# Revit family: Casement_41_C_Side_Hung_SD_Standard
name_source: partatom
category: Windows
revit_build: Autodesk Revit 2014 (Build: 20130308_1515(x64)
units: mm (PartAtom-declared; Revit-internal decimal feet)

## types (12) — shared parameters
Corrected Mullion Configuration = 2 mm  [stored 0.00656168 ft]
Custom Sash Width = 502 mm
Description = Window 41mm, Type C, Side hung, Standard sash
Frame Profile Thickness = 41 mm  [stored 0.134514 ft]
Heavy Duty Sash = No
Limit Fixed Pane Height Max = 3000 mm  [stored 9.84252 ft]
Limit Fixed Pane Height Min = 200 mm  [stored 0.656168 ft]
Limit Fixed Pane Width Max = 3000 mm  [stored 9.84252 ft]
Limit Fixed Pane Width Min = 200 mm  [stored 0.656168 ft]
Limit Sash Height Max = 1500 mm  [stored 4.92126 ft]
Limit Sash Height Min = 300 mm  [stored 0.984252 ft]
Limit Sash Width Max = 700 mm  [stored 2.29659 ft]
Limit Sash Width Min = 300 mm  [stored 0.984252 ft]
Limit Window Height Max = 1588 mm
Limit Window Height Min = 388 mm
Manufacturer = Crealco
Max System DG Unit Thickness = 25 mm  [stored 0.082021 ft]
Model = Casement 41
Rough Width = 3 mm  [stored 0.00984252 ft]
Sash Side Gap = 44 mm
Standard Mullion Different = No
Standard Sash = Yes
URL = http://www.crealco.co.za
Wall Closure = By host
zero-valued in all types: Custom Frame Offset From Exterior

## per-type parameters (varying)
| type | Clearvue Insulated LowE SHGC Value | Clearvue Insulated LowE U Value | Clearvue Insulated SHGC Value | Clearvue Insulated U Value | Clearvue SHGC Value | Clearvue U Value | Custom Windload | Custom Window Height | Custom Window Width | Energy Advantage SHGC Value | Energy Advantage U Value | Intruderprufe Insulated LowE SHGC Value | Intruderprufe Insulated LowE U Value | Intruderprufe Insulated SHGC Value | Intruderprufe Insulated U Value | Intruderprufe LowE SHGC Value | Intruderprufe LowE U Value | Intruderprufe SHGC Value | Intruderprufe U Value | Toughened Safety SHGC Value | Toughened Safety U Value |
| 41-1809SS-SD-1000Pa | 0.737 | 4.46 | 0.737 | 4.54 | 0.544 | 6.03 | 1000 mm  [stored 3.28084 ft] | 890 mm  [stored 2.91995 ft] | 1790 mm  [stored 5.8727 ft] | 0.49 | 4.86 | 0.612 | 3.2 | 0.612 | 3.26 | 0.456 | 4.74 | 0.513 | 5.92 | 0.544 | 6.03 |
| 41-1809SS-SD-1500Pa | 0.737 | 4.46 | 0.737 | 4.54 | 0.544 | 6.03 | 1500 mm  [stored 4.92126 ft] | 890 mm  [stored 2.91995 ft] | 1790 mm  [stored 5.8727 ft] | 0.49 | 4.86 | 0.612 | 3.2 | 0.612 | 3.26 | 0.456 | 4.74 | 0.513 | 5.92 | 0.544 | 6.03 |
| 41-1809SS-SD-2000Pa | 0.737 | 4.46 | 0.737 | 4.54 | 0.544 | 6.03 | 2000 mm  [stored 6.56168 ft] | 890 mm  [stored 2.91995 ft] | 1790 mm  [stored 5.8727 ft] | 0.49 | 4.86 | 0.612 | 3.2 | 0.612 | 3.26 | 0.456 | 4.74 | 0.513 | 5.92 | 0.544 | 6.03 |
| 41-2409SS-SD-1000Pa | 0.765 | 4.6 | 0.765 | 4.67 | 0.595 | 6.02 | 1000 mm  [stored 3.28084 ft] | 890 mm  [stored 2.91995 ft] | 2390 mm  [stored 7.84121 ft] | 0.534 | 4.68 | 0.635 | 3.18 | 0.635 | 3.22 | 0.496 | 4.55 | 0.56 | 5.87 | 0.595 | 6.02 |
| 41-2409SS-SD-1500Pa | 0.765 | 4.6 | 0.765 | 4.67 | 0.595 | 6.02 | 1500 mm  [stored 4.92126 ft] | 890 mm  [stored 2.91995 ft] | 2390 mm  [stored 7.84121 ft] | 0.534 | 4.68 | 0.635 | 3.18 | 0.635 | 3.22 | 0.496 | 4.55 | 0.56 | 5.87 | 0.595 | 6.02 |
| 41-2409SS-SD-2000Pa | 0.765 | 4.6 | 0.765 | 4.67 | 0.595 | 6.02 | 2000 mm  [stored 6.56168 ft] | 890 mm  [stored 2.91995 ft] | 2390 mm  [stored 7.84121 ft] | 0.534 | 4.68 | 0.635 | 3.18 | 0.635 | 3.22 | 0.496 | 4.55 | 0.56 | 5.87 | 0.595 | 6.02 |
| 41-1812SS-SD-1000Pa | 0.737 | 4.62 | 0.737 | 4.7 | 0.572 | 6.01 | 1000 mm  [stored 3.28084 ft] | 1190 mm  [stored 3.9042 ft] | 1790 mm  [stored 5.8727 ft] | 0.514 | 4.76 | 0.612 | 3.31 | 0.612 | 3.37 | 0.478 | 4.64 | 0.539 | 5.91 | 0.572 | 6.01 |
| 41-1812SS-SD-1500Pa | 0.737 | 4.62 | 0.737 | 4.7 | 0.572 | 6.01 | 1500 mm  [stored 4.92126 ft] | 1190 mm  [stored 3.9042 ft] | 1790 mm  [stored 5.8727 ft] | 0.514 | 4.76 | 0.612 | 3.31 | 0.612 | 3.37 | 0.478 | 4.64 | 0.539 | 5.91 | 0.572 | 6.01 |
| 41-1812SS-SD-2000Pa | 0.737 | 4.62 | 0.737 | 4.7 | 0.572 | 6.01 | 2000 mm  [stored 6.56168 ft] | 1190 mm  [stored 3.9042 ft] | 1790 mm  [stored 5.8727 ft] | 0.514 | 4.76 | 0.612 | 3.31 | 0.612 | 3.37 | 0.478 | 4.64 | 0.539 | 5.91 | 0.572 | 6.01 |
| 41-2412SS-SD-1000Pa | 0.765 | 4.78 | 0.765 | 4.84 | 0.622 | 5.99 | 1000 mm  [stored 3.28084 ft] | 1190 mm  [stored 3.9042 ft] | 2390 mm  [stored 7.84121 ft] | 0.558 | 4.57 | 0.635 | 3.29 | 0.635 | 3.34 | 0.519 | 4.46 | 0.586 | 5.87 | 0.622 | 5.99 |
| 41-2412SS-SD-1500Pa | 0.765 | 4.78 | 0.765 | 4.84 | 0.622 | 5.99 | 1500 mm  [stored 4.92126 ft] | 1190 mm  [stored 3.9042 ft] | 2390 mm  [stored 7.84121 ft] | 0.558 | 4.57 | 0.635 | 3.29 | 0.635 | 3.34 | 0.519 | 4.46 | 0.586 | 5.87 | 0.622 | 5.99 |
| 41-2412SS-SD-2000Pa | 0.765 | 4.78 | 0.765 | 4.84 | 0.622 | 5.99 | 2000 mm  [stored 6.56168 ft] | 1190 mm  [stored 3.9042 ft] | 2390 mm  [stored 7.84121 ft] | 0.558 | 4.57 | 0.635 | 3.29 | 0.635 | 3.34 | 0.519 | 4.46 | 0.586 | 5.87 | 0.622 | 5.99 |

note: [stored X ft] marks values corroborated as IEEE doubles in the binary element streams (Revit-internal decimal feet)

## geometry (parser evidence)
native form markers: Sweep x21
no freeform markers — native parametric forms only
